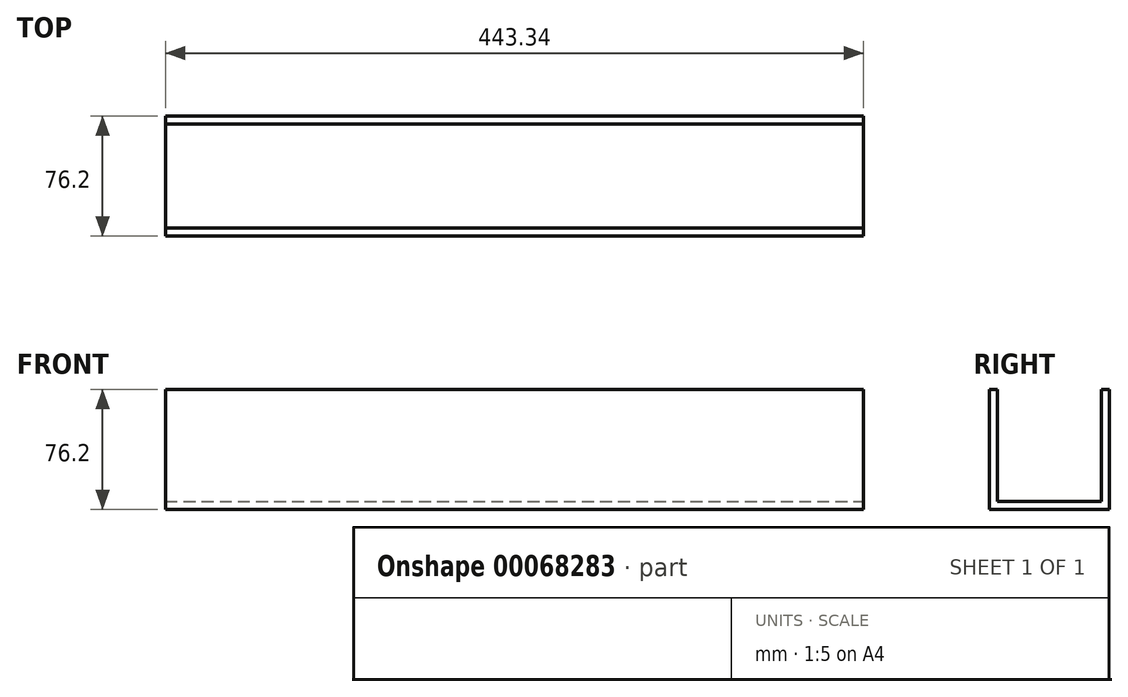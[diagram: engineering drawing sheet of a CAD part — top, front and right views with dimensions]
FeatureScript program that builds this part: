
annotation { "Feature Type Name" : "Feature", "Feature Type Description" : "" }
export const myFeature = defineFeature(function(context is Context, id is Id, definition is map)
    precondition{}
    {
        {
            var Q0;
            Q0=qCreatedBy(makeId("Top.planeOp"),FACE);
            var sketch = newSketch(context, id + "F0", { "sketchPlane" : qUnion([Q0])});
            skLineSegment(sketch, "E0.rect.bottom", {"start": v(-221.67, 38.1) * mm, "end": v(221.67, 38.1) * mm});
            skLineSegment(sketch, "E0.rect.top", {"start": v(-221.67, -38.1) * mm, "end": v(221.67, -38.1) * mm});
            skLineSegment(sketch, "E0.rect.left", {"start": v(-221.67, 38.1) * mm, "end": v(-221.67, -38.1) * mm});
            skLineSegment(sketch, "E0.rect.right", {"start": v(221.67, 38.1) * mm, "end": v(221.67, -38.1) * mm});
            skPoint(sketch, "E0.rect.middle", {"position": v(0, 0) * mm});
            skSolve(sketch);
        }
        {
            var Q0;
            Q0=qSketchRegion(id+"F0",true);
            extrude(context, id + "F1", {"entities" : qUnion([Q0]), "depth" : 76.2 * mm});
        }
        {
            var Q0;
            Q0=makeQuery(id+"F1.opExtrude","CAP_FACE",FACE,{"disambiguationData":[OSD([sQuery(id+"F0.wireOp",EDGE,"E0.rect.bottom"),sQuery(id+"F0.wireOp",EDGE,"E0.rect.top"),sQuery(id+"F0.wireOp",EDGE,"E0.rect.left"),sQuery(id+"F0.wireOp",EDGE,"E0.rect.right")])],"isStart":false});
            var Q1;
            Q1=makeQuery(id+"F1.opExtrude","SWEPT_FACE",FACE,{"disambiguationData":[OSD([sQuery(id+"F0.wireOp",EDGE,"E0.rect.left")])]});
            var Q2;
            Q2=makeQuery(id+"F1.opExtrude","SWEPT_FACE",FACE,{"disambiguationData":[OSD([sQuery(id+"F0.wireOp",EDGE,"E0.rect.right")])]});
            var Q3;
            Q3=makeQuery(id+"F1.opExtrude","SWEPT_BODY",BODY,{"disambiguationData":[OSD([sQuery(id+"F0.wireOp",EDGE,"E0.rect.bottom"),sQuery(id+"F0.wireOp",EDGE,"E0.rect.top"),sQuery(id+"F0.wireOp",EDGE,"E0.rect.left"),sQuery(id+"F0.wireOp",EDGE,"E0.rect.right")])]});
            shell(context, id + "F2", {"entities" : qUnion([Q0, Q1, Q2]), "parts" : qUnion([Q3]), "thickness" : 5.08 * mm});
        }
    });
